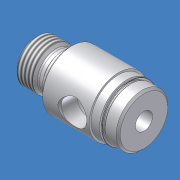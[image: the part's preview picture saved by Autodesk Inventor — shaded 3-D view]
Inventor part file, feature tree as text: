
AUTODESK INVENTOR PART (.ipt)
format: ipt  version: 2012 (Build 160160000, 160)  size: 240,640 bytes
history: native  units: mm (DEFAULTED — no unit token found)
features: other x106, revolve x6, sketch x6, thread x1
ambient origin geometry x8: Origin, YZ Plane, XZ Plane, XY Plane, X Axis, Y Axis, Z Axis, Center Point
bodies: Solid1 (feature_tree)
feature tree (119):
  other  "04R000_rod_guide"
  revolve  "Revolution1"  [1 undecoded]
  thread  "Thread1"  [1 undecoded]
  revolve  "Revolution2"  Angle=360.0deg
  revolve  "Revolution3"  Angle=360.0deg
  revolve  "Revolution4"  [1 undecoded]
  revolve  "Revolution5"  [1 undecoded]
  revolve  "Revolution6"  [1 undecoded]
  other  "s1_XY"
  other  "s1_YZ"
  other  "s1_ZX"
  other  "s1_X"
  other  "s1_Y"
  other  "s1_Z"
  other  "s1_Center"
  other  "s2_XY"
  other  "s2_YZ"
  other  "s2_ZX"
  other  "s2_X"
  other  "s2_Y"
  other  "s2_Z"
  other  "s2_Center"
  other  "dp1_XY"
  other  "dp1_YZ"
  other  "dp1_ZX"
  other  "dp1_X"
  other  "dp1_Y"
  other  "dp1_Z"
  other  "dp1_Center"
  other  "dp2_XY"
  other  "dp2_YZ"
  other  "dp2_ZX"
  other  "dp2_X"
  other  "dp2_Y"
  other  "dp2_Z"
  other  "dp2_Center"
  other  "rod_guide_XY"
  other  "rod_guide_YZ"
  other  "rod_guide_ZX"
  other  "rod_guide_X"
  other  "rod_guide_Y"
  other  "rod_guide_Z"
  other  "rod_guide_Center"
  other  "to_tube_XY"
  other  "to_tube_YZ"
  other  "to_tube_ZX"
  other  "to_tube_X"
  other  "to_tube_Y"
  other  "to_tube_Z"
  other  "to_tube_Center"
  other  "to_foot_bracket_XY"
  other  "to_foot_bracket_YZ"
  other  "to_foot_bracket_ZX"
  other  "to_foot_bracket_X"
  other  "to_foot_bracket_Y"
  other  "to_foot_bracket_Z"
  other  "to_foot_bracket_Center"
  other  "to_nut_XY"
  other  "to_nut_YZ"
  other  "to_nut_ZX"
  other  "to_nut_X"
  other  "to_nut_Y"
  other  "to_nut_Z"
  other  "to_nut_Center"
  other  "to_trunnion_brackets_XY"
  other  "to_trunnion_brackets_YZ"
  other  "to_trunnion_brackets_ZX"
  other  "to_trunnion_brackets_X"
  other  "to_trunnion_brackets_Y"
  other  "to_trunnion_brackets_Z"
  other  "to_trunnion_brackets_Center"
  other  "to_trunnion_brackets1_XY"
  other  "to_trunnion_brackets1_YZ"
  other  "to_trunnion_brackets1_ZX"
  other  "to_trunnion_brackets1_X"
  other  "to_trunnion_brackets1_Y"
  other  "to_trunnion_brackets1_Z"
  other  "to_trunnion_brackets1_Center"
  other  "to_trunnion_brackets2_XY"
  other  "to_trunnion_brackets2_YZ"
  other  "to_trunnion_brackets2_ZX"
  other  "to_trunnion_brackets2_X"
  other  "to_trunnion_brackets2_Y"
  other  "to_trunnion_brackets2_Z"
  other  "to_trunnion_brackets2_Center"
  other  "t111_XY"
  other  "t111_YZ"
  other  "t111_ZX"
  other  "t111_X"
  other  "t111_Y"
  other  "t111_Z"
  other  "t111_Center"
  other  "t1_XY"
  other  "t1_YZ"
  other  "t1_ZX"
  other  "t1_X"
  other  "t1_Y"
  other  "t1_Z"
  other  "t1_Center"
  other  "port_XY"
  other  "port_YZ"
  other  "port_ZX"
  other  "port_X"
  other  "port_Y"
  other  "port_Z"
  other  "port_Center"
  other  "to_screw_XY"
  other  "to_screw_YZ"
  other  "to_screw_ZX"
  other  "to_screw_X"
  other  "to_screw_Y"
  other  "to_screw_Z"
  other  "to_screw_Center"
  sketch  "Sketch_2"  dims[d0=360.0deg d1=5.842127mm d2=0.0mm d3=360.0deg]
  sketch  "Sketch_3"  dims[d4=360.0deg d5=360.0deg]
  sketch  "Sketch_5"  dims[d6=360.0deg d7=360.0deg]
  sketch  "Sketch_10"
  sketch  "Sketch_40"
  sketch  "Sketch_47"
note: 5 required parameter values undecoded (feature->parameter linkage not recoverable at this tier; creation-order binding heuristic only, values carry confidence <= 0.55)